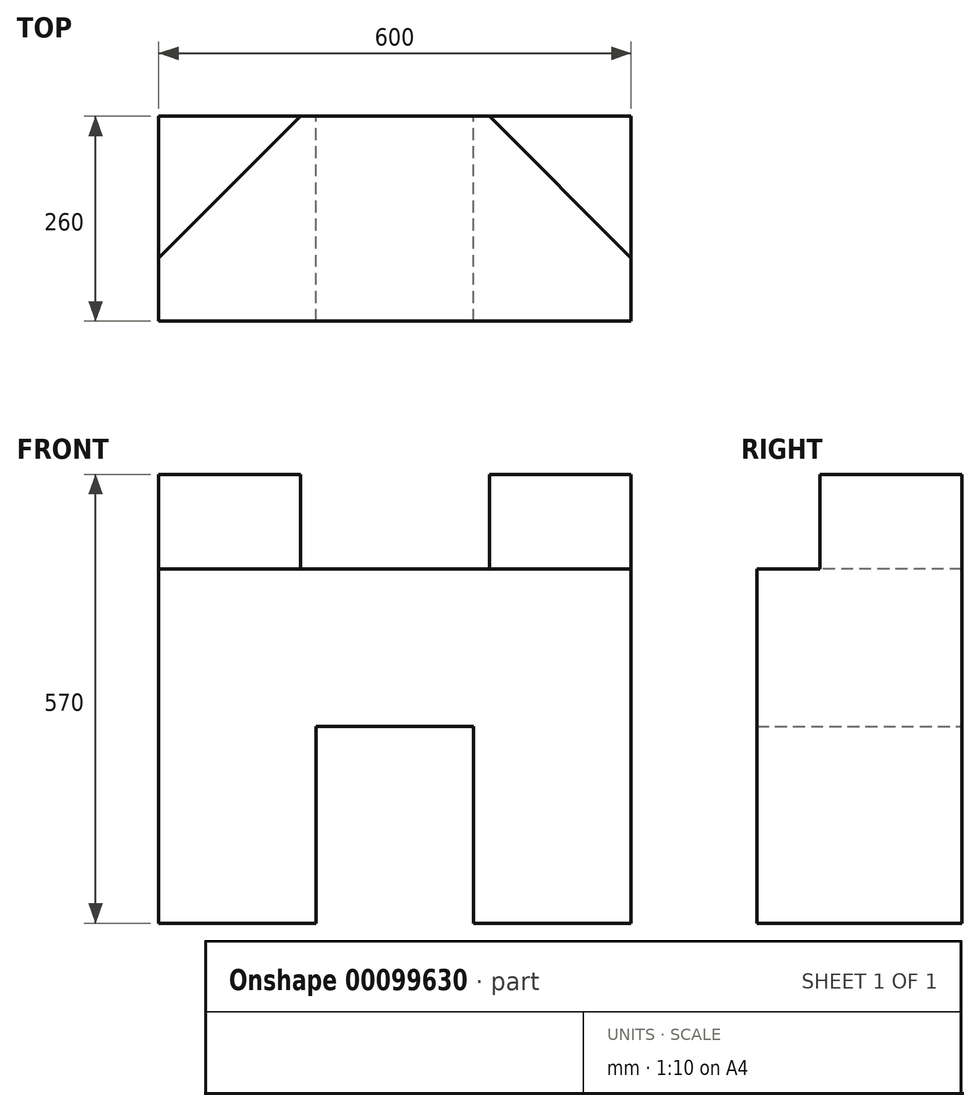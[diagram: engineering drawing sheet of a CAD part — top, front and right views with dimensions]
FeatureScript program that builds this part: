
annotation { "Feature Type Name" : "Feature", "Feature Type Description" : "" }
export const myFeature = defineFeature(function(context is Context, id is Id, definition is map)
    precondition{}
    {
        {
            var Q0;
            Q0=qCreatedBy(makeId("Front.planeOp"),FACE);
            var sketch = newSketch(context, id + "F0", { "sketchPlane" : qUnion([Q0])});
            skLineSegment(sketch, "E0.bottom", {"start": v(-300, 225) * mm, "end": v(300, 225) * mm});
            skLineSegment(sketch, "E0.top", {"start": v(-300, -225) * mm, "end": v(-100, -225) * mm});
            skLineSegment(sketch, "E0.left", {"start": v(-300, 225) * mm, "end": v(-300, -225) * mm});
            skLineSegment(sketch, "E0.right", {"start": v(300, 225) * mm, "end": v(300, -225) * mm});
            skPoint(sketch, "E0.middle", {"position": v(0, 0) * mm});
            skLineSegment(sketch, "E1.bottom", {"start": v(-100, 25) * mm, "end": v(100, 25) * mm});
            skLineSegment(sketch, "E1.left", {"start": v(-100, 25) * mm, "end": v(-100, -225) * mm});
            skLineSegment(sketch, "E1.right", {"start": v(100, 25) * mm, "end": v(100, -225) * mm});
            skPoint(sketch, "E1.middle", {"position": v(0, -225) * mm});
            skLineSegment(sketch, "E2.trimOffspring", {"start": v(100, -225) * mm, "end": v(300, -225) * mm});
            skPoint(sketch, "E1.top.end.orphan", {"position": v(100, -475) * mm});
            skPoint(sketch, "E3.orphan", {"position": v(-100, -475) * mm});
            skSolve(sketch);
        }
        {
            var Q0;
            Q0 = qSketchRegion(id + "F0", true);
            extrude(context, id + "F1", {"entities" : qUnion([Q0]), "depth" : 260 * mm});
        }
        {
            var Q0;
            Q0=makeQuery(id+"F1.opExtrude","SWEPT_FACE",FACE,{"disambiguationData":[OSD([sQuery(id+"F0.wireOp",EDGE,"E0.bottom")])]});
            var sketch = newSketch(context, id + "F2", { "sketchPlane" : qUnion([Q0])});
            skLineSegment(sketch, "E4", {"start": v(-120, 0) * mm, "end": v(-300, -180) * mm});
            skLineSegment(sketch, "E5", {"start": v(-300, 0) * mm, "end": v(-300, -180) * mm});
            skLineSegment(sketch, "E6", {"start": v(-300, 0) * mm, "end": v(-120, 0) * mm});
            skLineSegment(sketch, "E7", {"start": v(120, 0) * mm, "end": v(300, -180) * mm});
            skLineSegment(sketch, "E8", {"start": v(120, 0) * mm, "end": v(300, 0) * mm});
            skLineSegment(sketch, "E9", {"start": v(300, 0) * mm, "end": v(300, -180) * mm});
            skSolve(sketch);
        }
        {
            var Q0;
            Q0 = qSketchRegion(id + "F2", true);
            var Q1;
            Q1=makeQuery(id+"F2.imprint","IMPRINT",FACE,{"disambiguationData":[TD([[makeQuery(id+"F2.imprint","IMPRINT",EDGE,{"derivedFrom":sQuery(id+"F2.wireOp",EDGE,"E4")}),-1.0]])]});
            extrude(context, id + "F3", {"entities" : qUnion([Q0, Q1]), "operationType" : NewBodyOperationType.ADD, "depth" : 120 * mm});
        }
    });
